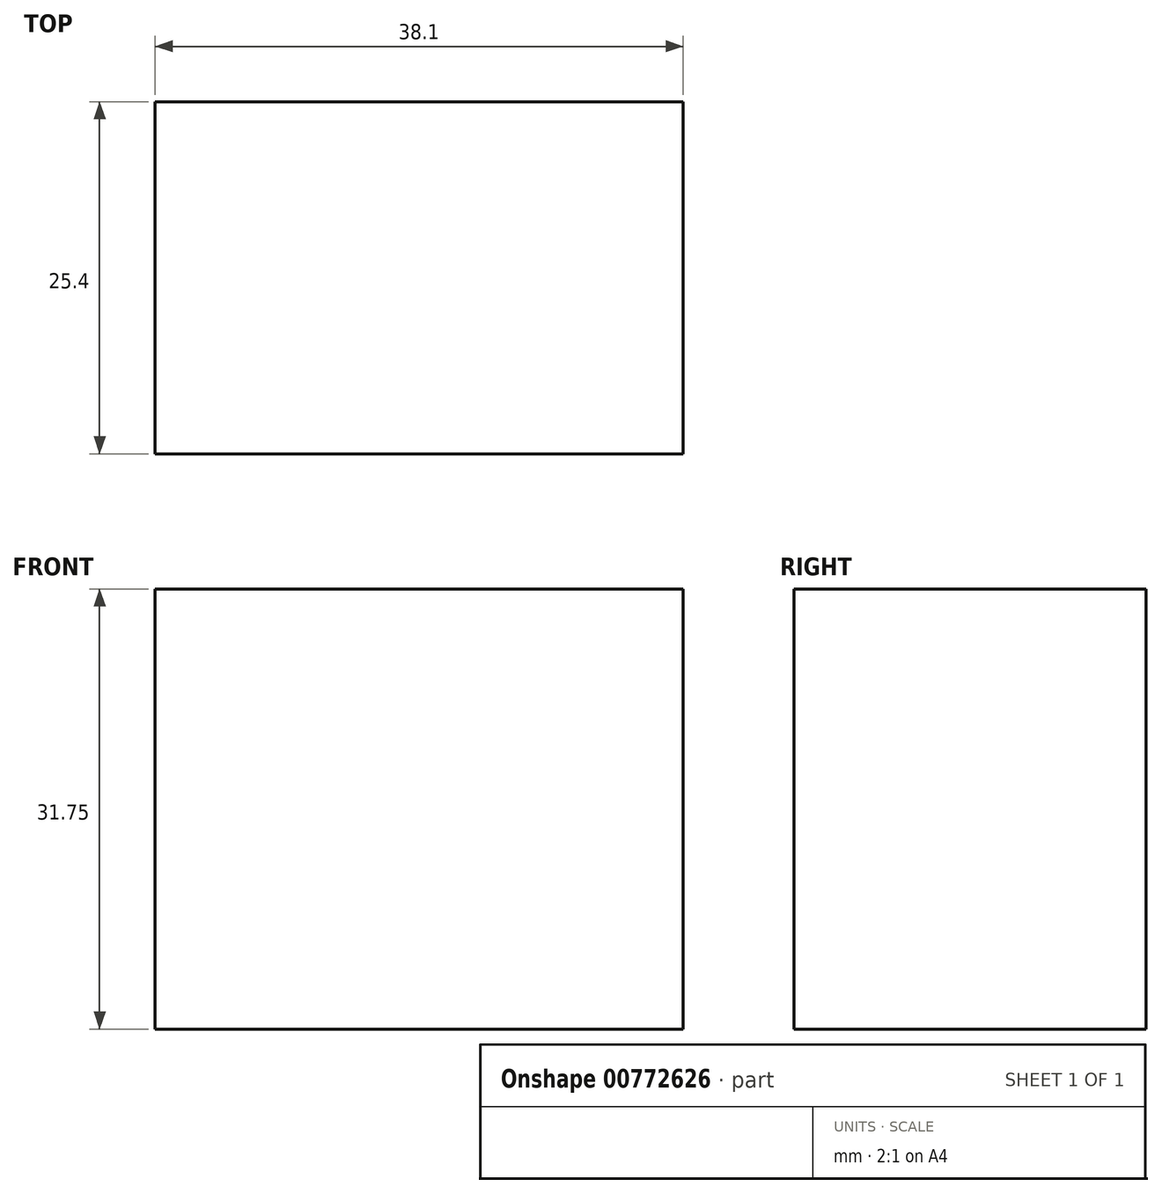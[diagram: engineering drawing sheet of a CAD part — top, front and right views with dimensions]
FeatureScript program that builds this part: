
annotation { "Feature Type Name" : "Feature", "Feature Type Description" : "" }
export const myFeature = defineFeature(function(context is Context, id is Id, definition is map)
    precondition{}
    {
        {
            var Q0;
            Q0=qCreatedBy(makeId("Front.planeOp"),FACE);
            var sketch = newSketch(context, id + "F0", { "sketchPlane" : qUnion([Q0])});
            skLineSegment(sketch, "E0", {"start": v(0, 0) * mm, "end": v(38.1, 0) * mm});
            skLineSegment(sketch, "E1", {"start": v(38.1, 0) * mm, "end": v(38.1, 31.75) * mm});
            skLineSegment(sketch, "E2", {"start": v(0, 0) * mm, "end": v(0, 31.75) * mm});
            skLineSegment(sketch, "E3", {"start": v(0, 31.75) * mm, "end": v(42.2, 31.75) * mm});
            skSolve(sketch);
        }
        {
            var Q0;
            Q0 = qSketchRegion(id + "F0", true);
            extrude(context, id + "F1", {"entities" : qUnion([Q0]), "depth" : 25.4 * mm, "offsetDistance" : 25.4 * mm});
        }
    });
